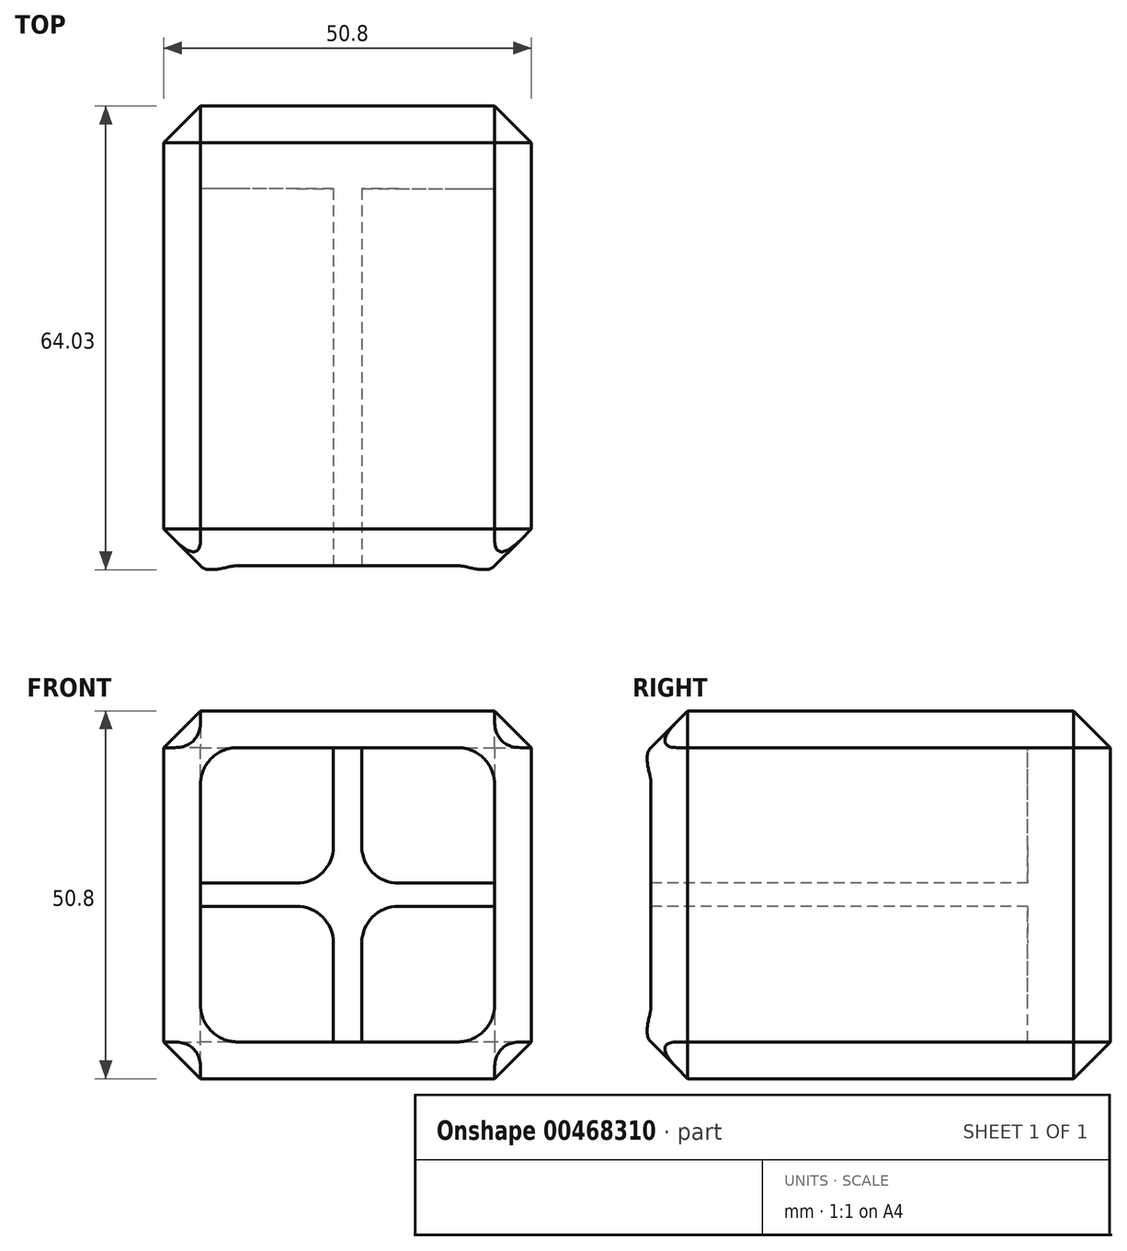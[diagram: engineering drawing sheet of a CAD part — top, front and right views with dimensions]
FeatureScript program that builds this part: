
annotation { "Feature Type Name" : "Feature", "Feature Type Description" : "" }
export const myFeature = defineFeature(function(context is Context, id is Id, definition is map)
    precondition{}
    {
        {
            var Q0;
            Q0=qCreatedBy(makeId("Front.planeOp"),FACE);
            var sketch = newSketch(context, id + "F0", { "sketchPlane" : qUnion([Q0])});
            skLineSegment(sketch, "E0.bottom", {"start": v(-25.4, -25.4) * mm, "end": v(25.4, -25.4) * mm});
            skLineSegment(sketch, "E0.top", {"start": v(-25.4, 25.4) * mm, "end": v(25.4, 25.4) * mm});
            skLineSegment(sketch, "E0.left", {"start": v(-25.4, -25.4) * mm, "end": v(-25.4, 25.4) * mm});
            skLineSegment(sketch, "E0.right", {"start": v(25.4, -25.4) * mm, "end": v(25.4, 25.4) * mm});
            skPoint(sketch, "E0.middle", {"position": v(0, 0) * mm});
            skSolve(sketch);
        }
        {
            var Q0;
            Q0=makeQuery(id+"F0.imprint","IMPRINT",FACE,{"disambiguationData":[TD([[makeQuery(id+"F0.imprint","IMPRINT",EDGE,{"derivedFrom":sQuery(id+"F0.wireOp",EDGE,"E0.bottom")}),1.0]])]});
            extrude(context, id + "F1", {"entities" : qUnion([Q0]), "depth" : 63.5 * mm});
        }
        {
            var Q0;
            Q0=makeQuery(id+"F1.opExtrude","SWEPT_FACE",FACE,{"disambiguationData":[OSD([sQuery(id+"F0.wireOp",EDGE,"E0.right")])]});
            var Q1;
            Q1=makeQuery(id+"F1.opExtrude","SWEPT_FACE",FACE,{"disambiguationData":[OSD([sQuery(id+"F0.wireOp",EDGE,"E0.top")])]});
            var Q2;
            Q2=makeQuery(id+"F1.opExtrude","SWEPT_FACE",FACE,{"disambiguationData":[OSD([sQuery(id+"F0.wireOp",EDGE,"E0.left")])]});
            var Q3;
            Q3=makeQuery(id+"F1.opExtrude","SWEPT_FACE",FACE,{"disambiguationData":[OSD([sQuery(id+"F0.wireOp",EDGE,"E0.bottom")])]});
            chamfer(context, id + "F2", {"entities" : qUnion([Q0, Q1, Q2, Q3]), "width" : 5.08 * mm, "tangentPropagation" : true});
        }
        {
            var Q0;
            Q0=makeQuery(id+"F1.opExtrude","CAP_FACE",FACE,{"disambiguationData":[OSD([sQuery(id+"F0.wireOp",EDGE,"E0.bottom"),sQuery(id+"F0.wireOp",EDGE,"E0.top"),sQuery(id+"F0.wireOp",EDGE,"E0.left"),sQuery(id+"F0.wireOp",EDGE,"E0.right")])],"isStart":false});
            var sketch = newSketch(context, id + "F3", { "sketchPlane" : qUnion([Q0])});
            skLineSegment(sketch, "E1", {"start": v(1.96, -20.32) * mm, "end": v(1.96, -1.59) * mm});
            skLineSegment(sketch, "E2", {"start": v(1.96, -1.59) * mm, "end": v(20.32, -1.59) * mm});
            skLineSegment(sketch, "E3.MirrorCS", {"start": v(-1.96, -1.59) * mm, "end": v(-20.32, -1.59) * mm});
            skLineSegment(sketch, "E4.MirrorCS", {"start": v(-1.96, -20.32) * mm, "end": v(-1.96, -1.59) * mm});
            skLineSegment(sketch, "E5", {"start": v(1.96, 1.6) * mm, "end": v(1.96, 20.32) * mm});
            skLineSegment(sketch, "E6", {"start": v(1.96, 1.6) * mm, "end": v(20.32, 1.6) * mm});
            skLineSegment(sketch, "E7.MirrorCS", {"start": v(-1.96, 1.6) * mm, "end": v(-1.96, 20.32) * mm});
            skLineSegment(sketch, "E8.MirrorCS", {"start": v(-1.96, 1.6) * mm, "end": v(-20.32, 1.6) * mm});
            skSolve(sketch);
        }
        {
            var Q0;
            {var subQ0=sQuery(id+"F3.wireOp",EDGE,"E1");Q0=makeQuery(id+"F3.imprint","IMPRINT",FACE,{"disambiguationData":[TD([[makeQuery(id+"F3.imprint","IMPRINT",EDGE,{"derivedFrom":subQ0}),-1.0]])]});}
            var Q1;
            {var subQ0=sQuery(id+"F3.wireOp",EDGE,"E5");Q1=makeQuery(id+"F3.imprint","IMPRINT",FACE,{"disambiguationData":[TD([[makeQuery(id+"F3.imprint","IMPRINT",EDGE,{"derivedFrom":subQ0}),-1.0]])]});}
            var Q2;
            {var subQ0=sQuery(id+"F3.wireOp",EDGE,"E7.MirrorCS");Q2=makeQuery(id+"F3.imprint","IMPRINT",FACE,{"disambiguationData":[TD([[makeQuery(id+"F3.imprint","IMPRINT",EDGE,{"derivedFrom":subQ0}),1.0]])]});}
            var Q3;
            {var subQ0=sQuery(id+"F3.wireOp",EDGE,"E3.MirrorCS");Q3=makeQuery(id+"F3.imprint","IMPRINT",FACE,{"disambiguationData":[TD([[makeQuery(id+"F3.imprint","IMPRINT",EDGE,{"derivedFrom":subQ0}),1.0]])]});}
            extrude(context, id + "F4", {"entities" : qUnion([Q0, Q1, Q2, Q3]), "operationType" : NewBodyOperationType.REMOVE, "oppositeDirection" : true, "depth" : 52.07 * mm});
        }
        {
            var Q0;
            Q0=makeQuery(id+"F4.boolean.opBoolean","COPY",EDGE,{"derivedFrom":makeQuery(id+"F4.opExtrude","SWEPT_EDGE",EDGE,{"disambiguationData":[OSD([sQuery(id+"F3.wireOp",EDGE,"E3.MirrorCS"),sQuery(id+"F3.wireOp",EDGE,"E4.MirrorCS")])]})});
            var Q1;
            Q1=makeQuery(id+"F4.boolean.opBoolean","COPY",EDGE,{"derivedFrom":makeQuery(id+"F4.opExtrude","SWEPT_EDGE",EDGE,{"disambiguationData":[OSD([sQuery(id+"F3.wireOp",EDGE,"E1"),sQuery(id+"F3.wireOp",EDGE,"E2")])]})});
            var Q2;
            Q2=makeQuery(id+"F4.boolean.opBoolean","COPY",EDGE,{"derivedFrom":makeQuery(id+"F4.opExtrude","SWEPT_EDGE",EDGE,{"disambiguationData":[OSD([sQuery(id+"F3.wireOp",EDGE,"E7.MirrorCS"),sQuery(id+"F3.wireOp",EDGE,"E8.MirrorCS")])]})});
            var Q3;
            Q3=makeQuery(id+"F4.boolean.opBoolean","COPY",EDGE,{"derivedFrom":makeQuery(id+"F4.opExtrude","SWEPT_EDGE",EDGE,{"disambiguationData":[OSD([sQuery(id+"F3.wireOp",EDGE,"E5"),sQuery(id+"F3.wireOp",EDGE,"E6")])]})});
            var Q4;
            {var subQ0=sQuery(id+"F0.wireOp",EDGE,"E0.right");var subQ1=sQuery(id+"F0.wireOp",EDGE,"E0.left");var subQ2=sQuery(id+"F0.wireOp",EDGE,"E0.top");var subQ3=sQuery(id+"F0.wireOp",EDGE,"E0.bottom");var subQ4=makeQuery(id+"F1.opExtrude","CAP_FACE",FACE,{"disambiguationData":[OSD([subQ3,subQ2,subQ1,subQ0])],"isStart":false});Q4=makeQuery(id+"F4.boolean.opBoolean","COPY",EDGE,{"derivedFrom":makeQuery(id+"F4.opExtrude","SWEPT_EDGE",EDGE,{"disambiguationData":[OSD([subQ3,subQ2,subQ1,subQ0]),TDD([makeQuery(id+"F3.imprint","INTERSECT",VERTEX,{"derivedFrom":[makeQuery(id+"F2.opChamfer","BLEND_EDGE",EDGE,{"blendedFrom":[makeQuery(id+"F1.opExtrude","CAP_EDGE",EDGE,{"disambiguationData":[OSD([subQ2])],"isStart":false}),subQ4],"blendedInto":[subQ4]}),makeQuery(id+"F2.opChamfer","BLEND_EDGE",EDGE,{"blendedFrom":[makeQuery(id+"F1.opExtrude","CAP_EDGE",EDGE,{"disambiguationData":[OSD([subQ1])],"isStart":false}),subQ4],"blendedInto":[subQ4]})]})])]})});}
            var Q5;
            {var subQ0=sQuery(id+"F0.wireOp",EDGE,"E0.right");var subQ1=sQuery(id+"F0.wireOp",EDGE,"E0.left");var subQ2=sQuery(id+"F0.wireOp",EDGE,"E0.top");var subQ3=sQuery(id+"F0.wireOp",EDGE,"E0.bottom");var subQ4=makeQuery(id+"F1.opExtrude","CAP_FACE",FACE,{"disambiguationData":[OSD([subQ3,subQ2,subQ1,subQ0])],"isStart":false});Q5=makeQuery(id+"F4.boolean.opBoolean","COPY",EDGE,{"derivedFrom":makeQuery(id+"F4.opExtrude","SWEPT_EDGE",EDGE,{"disambiguationData":[OSD([subQ3,subQ2,subQ1,subQ0]),TDD([makeQuery(id+"F3.imprint","INTERSECT",VERTEX,{"derivedFrom":[makeQuery(id+"F2.opChamfer","BLEND_EDGE",EDGE,{"blendedFrom":[makeQuery(id+"F1.opExtrude","CAP_EDGE",EDGE,{"disambiguationData":[OSD([subQ2])],"isStart":false}),subQ4],"blendedInto":[subQ4]}),makeQuery(id+"F2.opChamfer","BLEND_EDGE",EDGE,{"blendedFrom":[makeQuery(id+"F1.opExtrude","CAP_EDGE",EDGE,{"disambiguationData":[OSD([subQ0])],"isStart":false}),subQ4],"blendedInto":[subQ4]})]})])]})});}
            var Q6;
            {var subQ0=sQuery(id+"F0.wireOp",EDGE,"E0.right");var subQ1=sQuery(id+"F0.wireOp",EDGE,"E0.left");var subQ2=sQuery(id+"F0.wireOp",EDGE,"E0.top");var subQ3=sQuery(id+"F0.wireOp",EDGE,"E0.bottom");var subQ4=makeQuery(id+"F1.opExtrude","CAP_FACE",FACE,{"disambiguationData":[OSD([subQ3,subQ2,subQ1,subQ0])],"isStart":false});Q6=makeQuery(id+"F4.boolean.opBoolean","COPY",EDGE,{"derivedFrom":makeQuery(id+"F4.opExtrude","SWEPT_EDGE",EDGE,{"disambiguationData":[OSD([subQ3,subQ2,subQ1,subQ0]),TDD([makeQuery(id+"F3.imprint","INTERSECT",VERTEX,{"derivedFrom":[makeQuery(id+"F2.opChamfer","BLEND_EDGE",EDGE,{"blendedFrom":[makeQuery(id+"F1.opExtrude","CAP_EDGE",EDGE,{"disambiguationData":[OSD([subQ3])],"isStart":false}),subQ4],"blendedInto":[subQ4]}),makeQuery(id+"F2.opChamfer","BLEND_EDGE",EDGE,{"blendedFrom":[makeQuery(id+"F1.opExtrude","CAP_EDGE",EDGE,{"disambiguationData":[OSD([subQ0])],"isStart":false}),subQ4],"blendedInto":[subQ4]})]})])]})});}
            var Q7;
            {var subQ0=sQuery(id+"F0.wireOp",EDGE,"E0.right");var subQ1=sQuery(id+"F0.wireOp",EDGE,"E0.left");var subQ2=sQuery(id+"F0.wireOp",EDGE,"E0.top");var subQ3=sQuery(id+"F0.wireOp",EDGE,"E0.bottom");var subQ4=makeQuery(id+"F1.opExtrude","CAP_FACE",FACE,{"disambiguationData":[OSD([subQ3,subQ2,subQ1,subQ0])],"isStart":false});Q7=makeQuery(id+"F4.boolean.opBoolean","COPY",EDGE,{"derivedFrom":makeQuery(id+"F4.opExtrude","SWEPT_EDGE",EDGE,{"disambiguationData":[OSD([subQ3,subQ2,subQ1,subQ0]),TDD([makeQuery(id+"F3.imprint","INTERSECT",VERTEX,{"derivedFrom":[makeQuery(id+"F2.opChamfer","BLEND_EDGE",EDGE,{"blendedFrom":[makeQuery(id+"F1.opExtrude","CAP_EDGE",EDGE,{"disambiguationData":[OSD([subQ3])],"isStart":false}),subQ4],"blendedInto":[subQ4]}),makeQuery(id+"F2.opChamfer","BLEND_EDGE",EDGE,{"blendedFrom":[makeQuery(id+"F1.opExtrude","CAP_EDGE",EDGE,{"disambiguationData":[OSD([subQ1])],"isStart":false}),subQ4],"blendedInto":[subQ4]})]})])]})});}
            fillet(context, id + "F5", {"entities" : qUnion([Q0, Q1, Q2, Q3, Q4, Q5, Q6, Q7]), "radius" : 5.08 * mm, "tangentPropagation" : true, "allowEdgeOverflow" : false});
        }
        {
            var Q0;
            {var subQ0=sQuery(id+"F0.wireOp",EDGE,"E0.right");var subQ1=sQuery(id+"F0.wireOp",EDGE,"E0.left");var subQ2=sQuery(id+"F0.wireOp",EDGE,"E0.top");var subQ3=sQuery(id+"F0.wireOp",EDGE,"E0.bottom");var subQ4=makeQuery(id+"F1.opExtrude","CAP_FACE",FACE,{"disambiguationData":[OSD([subQ3,subQ2,subQ1,subQ0])],"isStart":false});var subQ5=makeQuery(id+"F1.opExtrude","CAP_EDGE",EDGE,{"disambiguationData":[OSD([subQ0])],"isStart":false});var subQ6=makeQuery(id+"F1.opExtrude","CAP_EDGE",EDGE,{"disambiguationData":[OSD([subQ3])],"isStart":false});Q0=makeQuery(id+"F5.opFillet","TWEAK_EDGE",EDGE,{"derivedFrom":[makeQuery(id+"F4.boolean.opBoolean","MERGE",VERTEX,{"derivedFrom":[makeQuery(id+"F2.opChamfer","BLEND_VERTEX",VERTEX,{"blendedFrom":[makeQuery(id+"F1.opExtrude","CAP_VERTEX",VERTEX,{"disambiguationData":[OSD([subQ3,subQ0])],"isStart":false}),subQ6,subQ5,subQ4],"blendedInto":[subQ4]}),makeQuery(id+"F4.opExtrude","CAP_VERTEX",VERTEX,{"disambiguationData":[OSD([subQ3,subQ2,subQ1,subQ0]),TDD([makeQuery(id+"F3.imprint","INTERSECT",VERTEX,{"derivedFrom":[makeQuery(id+"F2.opChamfer","BLEND_EDGE",EDGE,{"blendedFrom":[subQ6,subQ4],"blendedInto":[subQ4]}),makeQuery(id+"F2.opChamfer","BLEND_EDGE",EDGE,{"blendedFrom":[subQ5,subQ4],"blendedInto":[subQ4]})]})])],"isStart":true})]})]});}
            var Q1;
            {var subQ0=sQuery(id+"F0.wireOp",EDGE,"E0.right");var subQ1=sQuery(id+"F0.wireOp",EDGE,"E0.left");var subQ2=sQuery(id+"F0.wireOp",EDGE,"E0.top");var subQ3=sQuery(id+"F0.wireOp",EDGE,"E0.bottom");var subQ4=makeQuery(id+"F1.opExtrude","CAP_FACE",FACE,{"disambiguationData":[OSD([subQ3,subQ2,subQ1,subQ0])],"isStart":false});var subQ5=makeQuery(id+"F1.opExtrude","CAP_EDGE",EDGE,{"disambiguationData":[OSD([subQ0])],"isStart":false});var subQ6=makeQuery(id+"F1.opExtrude","CAP_EDGE",EDGE,{"disambiguationData":[OSD([subQ2])],"isStart":false});Q1=makeQuery(id+"F5.opFillet","TWEAK_EDGE",EDGE,{"derivedFrom":[makeQuery(id+"F4.boolean.opBoolean","MERGE",VERTEX,{"derivedFrom":[makeQuery(id+"F2.opChamfer","BLEND_VERTEX",VERTEX,{"blendedFrom":[makeQuery(id+"F1.opExtrude","CAP_VERTEX",VERTEX,{"disambiguationData":[OSD([subQ2,subQ0])],"isStart":false}),subQ6,subQ5,subQ4],"blendedInto":[subQ4]}),makeQuery(id+"F4.opExtrude","CAP_VERTEX",VERTEX,{"disambiguationData":[OSD([subQ3,subQ2,subQ1,subQ0]),TDD([makeQuery(id+"F3.imprint","INTERSECT",VERTEX,{"derivedFrom":[makeQuery(id+"F2.opChamfer","BLEND_EDGE",EDGE,{"blendedFrom":[subQ6,subQ4],"blendedInto":[subQ4]}),makeQuery(id+"F2.opChamfer","BLEND_EDGE",EDGE,{"blendedFrom":[subQ5,subQ4],"blendedInto":[subQ4]})]})])],"isStart":true})]})]});}
            var Q2;
            {var subQ0=sQuery(id+"F0.wireOp",EDGE,"E0.right");var subQ1=sQuery(id+"F0.wireOp",EDGE,"E0.left");var subQ2=sQuery(id+"F0.wireOp",EDGE,"E0.top");var subQ3=sQuery(id+"F0.wireOp",EDGE,"E0.bottom");var subQ4=makeQuery(id+"F1.opExtrude","CAP_FACE",FACE,{"disambiguationData":[OSD([subQ3,subQ2,subQ1,subQ0])],"isStart":false});var subQ5=makeQuery(id+"F1.opExtrude","CAP_EDGE",EDGE,{"disambiguationData":[OSD([subQ1])],"isStart":false});var subQ6=makeQuery(id+"F1.opExtrude","CAP_EDGE",EDGE,{"disambiguationData":[OSD([subQ2])],"isStart":false});Q2=makeQuery(id+"F5.opFillet","TWEAK_EDGE",EDGE,{"derivedFrom":[makeQuery(id+"F4.boolean.opBoolean","MERGE",VERTEX,{"derivedFrom":[makeQuery(id+"F2.opChamfer","BLEND_VERTEX",VERTEX,{"blendedFrom":[makeQuery(id+"F1.opExtrude","CAP_VERTEX",VERTEX,{"disambiguationData":[OSD([subQ2,subQ1])],"isStart":false}),subQ6,subQ5,subQ4],"blendedInto":[subQ4]}),makeQuery(id+"F4.opExtrude","CAP_VERTEX",VERTEX,{"disambiguationData":[OSD([subQ3,subQ2,subQ1,subQ0]),TDD([makeQuery(id+"F3.imprint","INTERSECT",VERTEX,{"derivedFrom":[makeQuery(id+"F2.opChamfer","BLEND_EDGE",EDGE,{"blendedFrom":[subQ6,subQ4],"blendedInto":[subQ4]}),makeQuery(id+"F2.opChamfer","BLEND_EDGE",EDGE,{"blendedFrom":[subQ5,subQ4],"blendedInto":[subQ4]})]})])],"isStart":true})]})]});}
            var Q3;
            {var subQ0=sQuery(id+"F0.wireOp",EDGE,"E0.right");var subQ1=sQuery(id+"F0.wireOp",EDGE,"E0.left");var subQ2=sQuery(id+"F0.wireOp",EDGE,"E0.top");var subQ3=sQuery(id+"F0.wireOp",EDGE,"E0.bottom");var subQ4=makeQuery(id+"F1.opExtrude","CAP_FACE",FACE,{"disambiguationData":[OSD([subQ3,subQ2,subQ1,subQ0])],"isStart":false});var subQ5=makeQuery(id+"F1.opExtrude","CAP_EDGE",EDGE,{"disambiguationData":[OSD([subQ1])],"isStart":false});var subQ6=makeQuery(id+"F1.opExtrude","CAP_EDGE",EDGE,{"disambiguationData":[OSD([subQ3])],"isStart":false});Q3=makeQuery(id+"F5.opFillet","TWEAK_EDGE",EDGE,{"derivedFrom":[makeQuery(id+"F4.boolean.opBoolean","MERGE",VERTEX,{"derivedFrom":[makeQuery(id+"F2.opChamfer","BLEND_VERTEX",VERTEX,{"blendedFrom":[makeQuery(id+"F1.opExtrude","CAP_VERTEX",VERTEX,{"disambiguationData":[OSD([subQ3,subQ1])],"isStart":false}),subQ6,subQ5,subQ4],"blendedInto":[subQ4]}),makeQuery(id+"F4.opExtrude","CAP_VERTEX",VERTEX,{"disambiguationData":[OSD([subQ3,subQ2,subQ1,subQ0]),TDD([makeQuery(id+"F3.imprint","INTERSECT",VERTEX,{"derivedFrom":[makeQuery(id+"F2.opChamfer","BLEND_EDGE",EDGE,{"blendedFrom":[subQ6,subQ4],"blendedInto":[subQ4]}),makeQuery(id+"F2.opChamfer","BLEND_EDGE",EDGE,{"blendedFrom":[subQ5,subQ4],"blendedInto":[subQ4]})]})])],"isStart":true})]})]});}
            fillet(context, id + "F6", {"entities" : qUnion([Q0, Q1, Q2, Q3]), "radius" : 5.08 * mm, "tangentPropagation" : true, "allowEdgeOverflow" : false});
        }
    });
